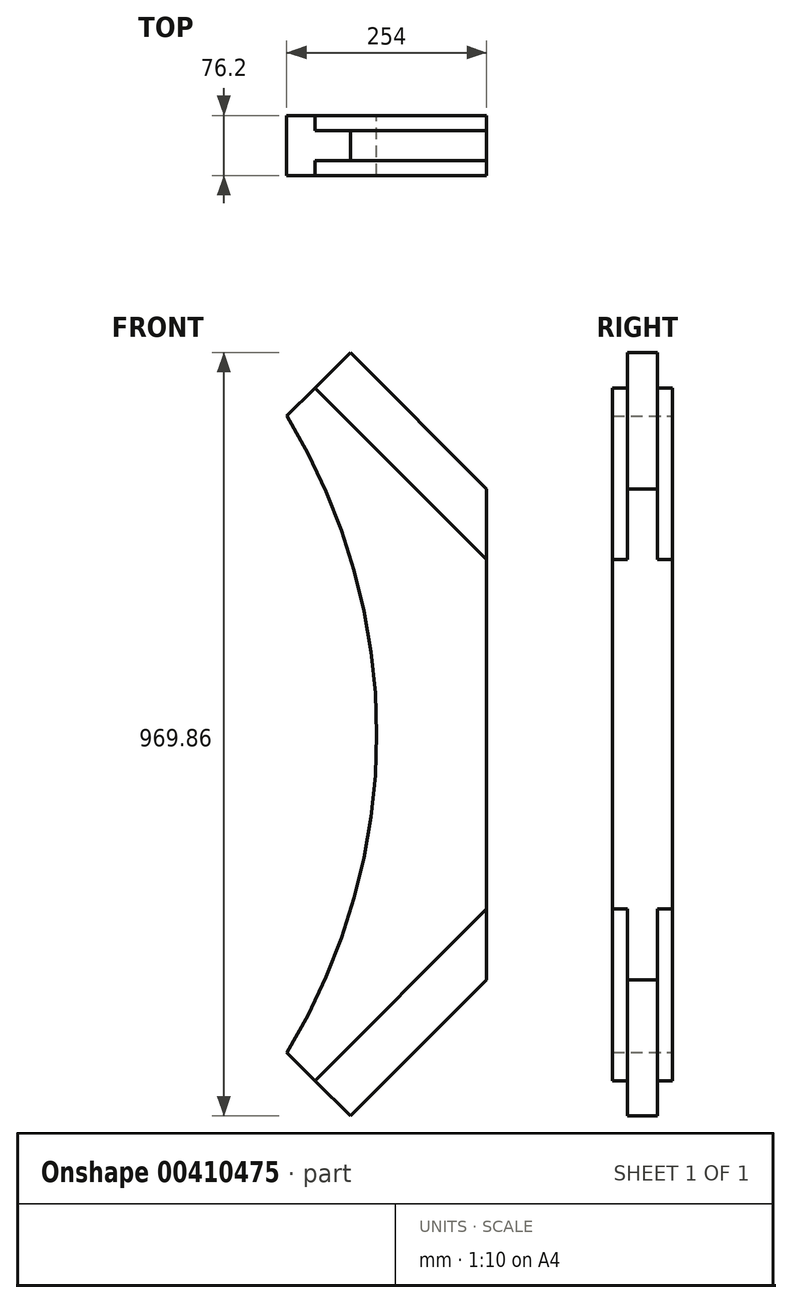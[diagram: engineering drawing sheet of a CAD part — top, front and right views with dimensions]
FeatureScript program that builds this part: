
annotation { "Feature Type Name" : "Feature", "Feature Type Description" : "" }
export const myFeature = defineFeature(function(context is Context, id is Id, definition is map)
    precondition{}
    {
        {
            var Q0;
            Q0=qCreatedBy(makeId("Front.planeOp"),FACE);
            var sketch = newSketch(context, id + "F0", { "sketchPlane" : qUnion([Q0])});
            skLineSegment(sketch, "E0.bottom", {"start": v(-127, 698.5) * mm, "end": v(127, 698.5) * mm});
            skLineSegment(sketch, "E0.top", {"start": v(-127, -698.5) * mm, "end": v(127, -698.5) * mm});
            skLineSegment(sketch, "E0.left", {"start": v(-127, 698.5) * mm, "end": v(-127, -698.5) * mm});
            skLineSegment(sketch, "E0.right", {"start": v(127, 698.5) * mm, "end": v(127, -698.5) * mm});
            skPoint(sketch, "E0.middle", {"position": v(0, 0) * mm});
            skLineSegment(sketch, "E1", {"start": v(-127, 543.35) * mm, "end": v(127, 289.35) * mm});
            skLineSegment(sketch, "E2", {"start": v(-127, 543.35) * mm, "end": v(-46.18, 624.17) * mm});
            skLineSegment(sketch, "E3", {"start": v(-46.18, 624.17) * mm, "end": v(127, 451) * mm});
            skLineSegment(sketch, "E4", {"start": v(-91.08, 579.27) * mm, "end": v(127, 361.2) * mm});
            skLineSegment(sketch, "E5", {"start": v(127, -10.87) * mm, "end": v(-127, -264.87) * mm});
            skLineSegment(sketch, "E6", {"start": v(-127, -264.87) * mm, "end": v(-46.18, -345.7) * mm});
            skLineSegment(sketch, "E7", {"start": v(-46.18, -345.7) * mm, "end": v(127, -172.51) * mm});
            skLineSegment(sketch, "E8", {"start": v(127, -82.71) * mm, "end": v(-91.08, -300.8) * mm});
            skArc(sketch, "E9", {"start": v(-127, -264.87) * mm, "mid": v(-12.7, 139.24) * mm, "end": v(-127, 543.35) * mm});
            skLineSegment(sketch, "E10", {"start": v(-100.06, -291.8) * mm, "end": v(127, -64.75) * mm});
            skLineSegment(sketch, "E11", {"start": v(-100.06, 570.3) * mm, "end": v(127, 343.23) * mm});
            skSolve(sketch);
        }
        {
            var Q0;
            {var subQ0=sQuery(id+"F0.wireOp",EDGE,"E1");Q0=makeQuery(id+"F0.imprint","IMPRINT",FACE,{"disambiguationData":[TD([[makeQuery(id+"F0.imprint","IMPRINT",EDGE,{"derivedFrom":subQ0}),-1.0]])]});}
            var Q1;
            {var subQ0=sQuery(id+"F0.wireOp",EDGE,"E5");Q1=makeQuery(id+"F0.imprint","IMPRINT",FACE,{"disambiguationData":[TD([[makeQuery(id+"F0.imprint","IMPRINT",EDGE,{"derivedFrom":subQ0}),1.0]])]});}
            var Q2;
            {var subQ0=sQuery(id+"F0.wireOp",EDGE,"E1");Q2=makeQuery(id+"F0.imprint","IMPRINT",FACE,{"disambiguationData":[TD([[makeQuery(id+"F0.imprint","IMPRINT",EDGE,{"derivedFrom":subQ0}),1.0]])]});}
            var Q3;
            {var subQ0=sQuery(id+"F0.wireOp",EDGE,"E4");Q3=makeQuery(id+"F0.imprint","IMPRINT",FACE,{"disambiguationData":[TD([[makeQuery(id+"F0.imprint","IMPRINT",EDGE,{"derivedFrom":subQ0}),-1.0]])]});}
            var Q4;
            {var subQ0=sQuery(id+"F0.wireOp",EDGE,"E8");Q4=makeQuery(id+"F0.imprint","IMPRINT",FACE,{"disambiguationData":[TD([[makeQuery(id+"F0.imprint","IMPRINT",EDGE,{"derivedFrom":subQ0}),-1.0]])]});}
            extrude(context, id + "F1", {"entities" : qUnion([Q0, Q1, Q2, Q3, Q4]), "depth" : 76.2 * mm, "offsetDistance" : 25.4 * mm, "symmetric" : true});
        }
        {
            var Q0;
            {var subQ0=sQuery(id+"F0.wireOp",EDGE,"E3");Q0=makeQuery(id+"F0.imprint","IMPRINT",FACE,{"disambiguationData":[TD([[makeQuery(id+"F0.imprint","IMPRINT",EDGE,{"derivedFrom":subQ0}),-1.0]])]});}
            var Q1;
            {var subQ0=sQuery(id+"F0.wireOp",EDGE,"E7");Q1=makeQuery(id+"F0.imprint","IMPRINT",FACE,{"disambiguationData":[TD([[makeQuery(id+"F0.imprint","IMPRINT",EDGE,{"derivedFrom":subQ0}),1.0]])]});}
            extrude(context, id + "F2", {"entities" : qUnion([Q0, Q1]), "operationType" : NewBodyOperationType.ADD, "depth" : 38.1 * mm, "offsetDistance" : 25.4 * mm, "symmetric" : true});
        }
    });
